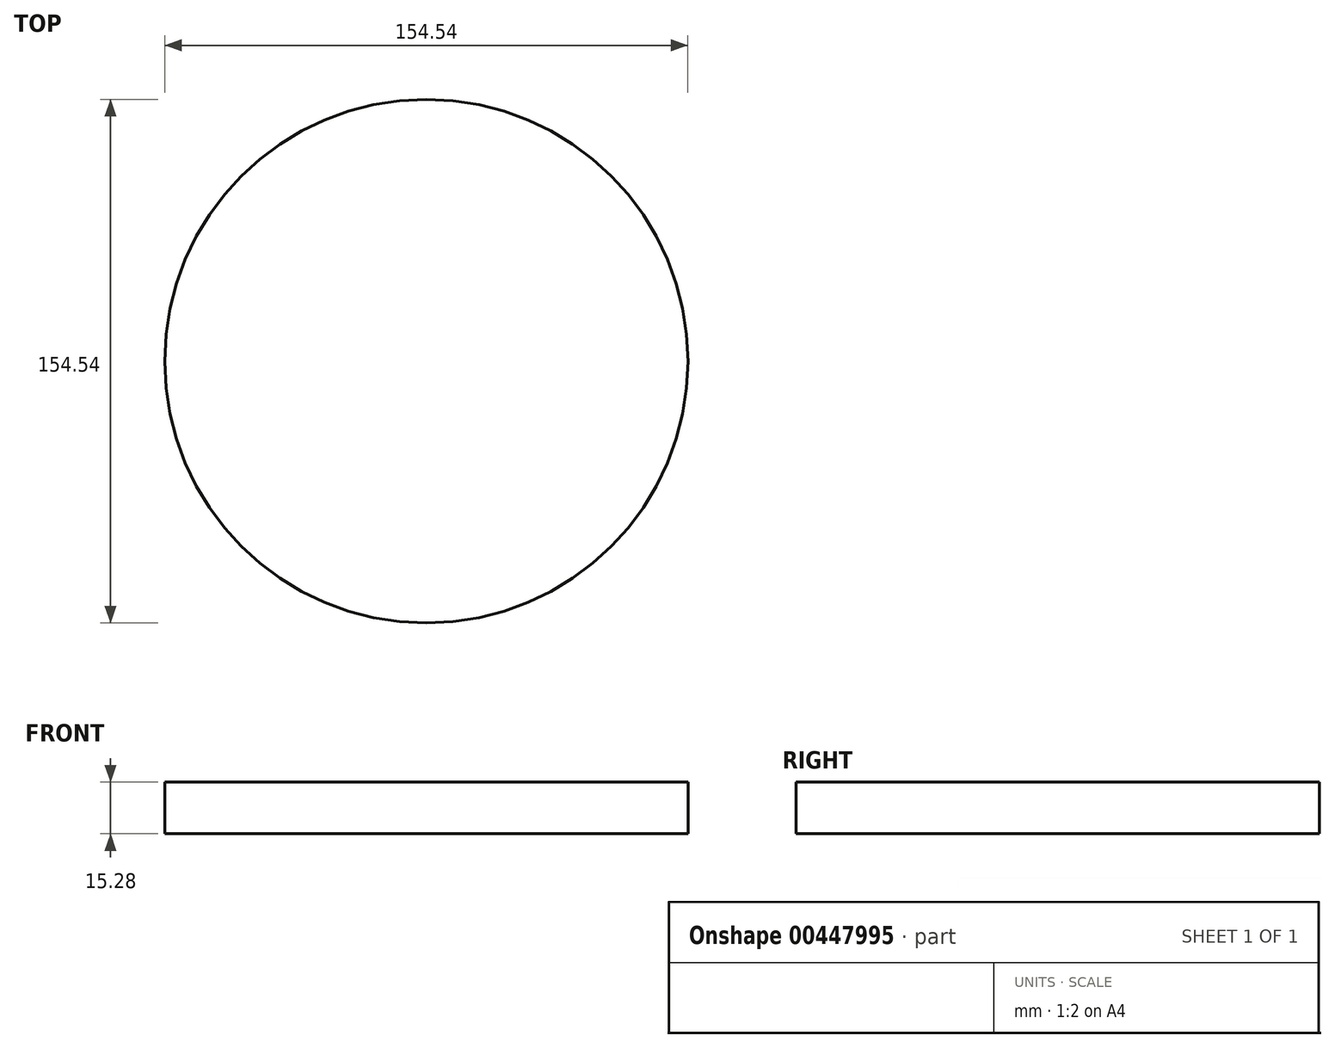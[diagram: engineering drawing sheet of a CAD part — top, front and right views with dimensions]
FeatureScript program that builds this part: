
annotation { "Feature Type Name" : "Feature", "Feature Type Description" : "" }
export const myFeature = defineFeature(function(context is Context, id is Id, definition is map)
    precondition{}
    {
        {
            var Q0;
            Q0=qCreatedBy(makeId("Top.planeOp"),FACE);
            var sketch = newSketch(context, id + "F0", { "sketchPlane" : qUnion([Q0])});
            skCircle(sketch, "E0", {"center": v(0, 0) * mm, "radius": 77.27 * mm});
            skSolve(sketch);
        }
        {
            var Q0;
            Q0 = qSketchRegion(id + "F0", true);
            extrude(context, id + "F1", {"entities" : qUnion([Q0]), "depth" : 15.28 * mm});
        }
    });
